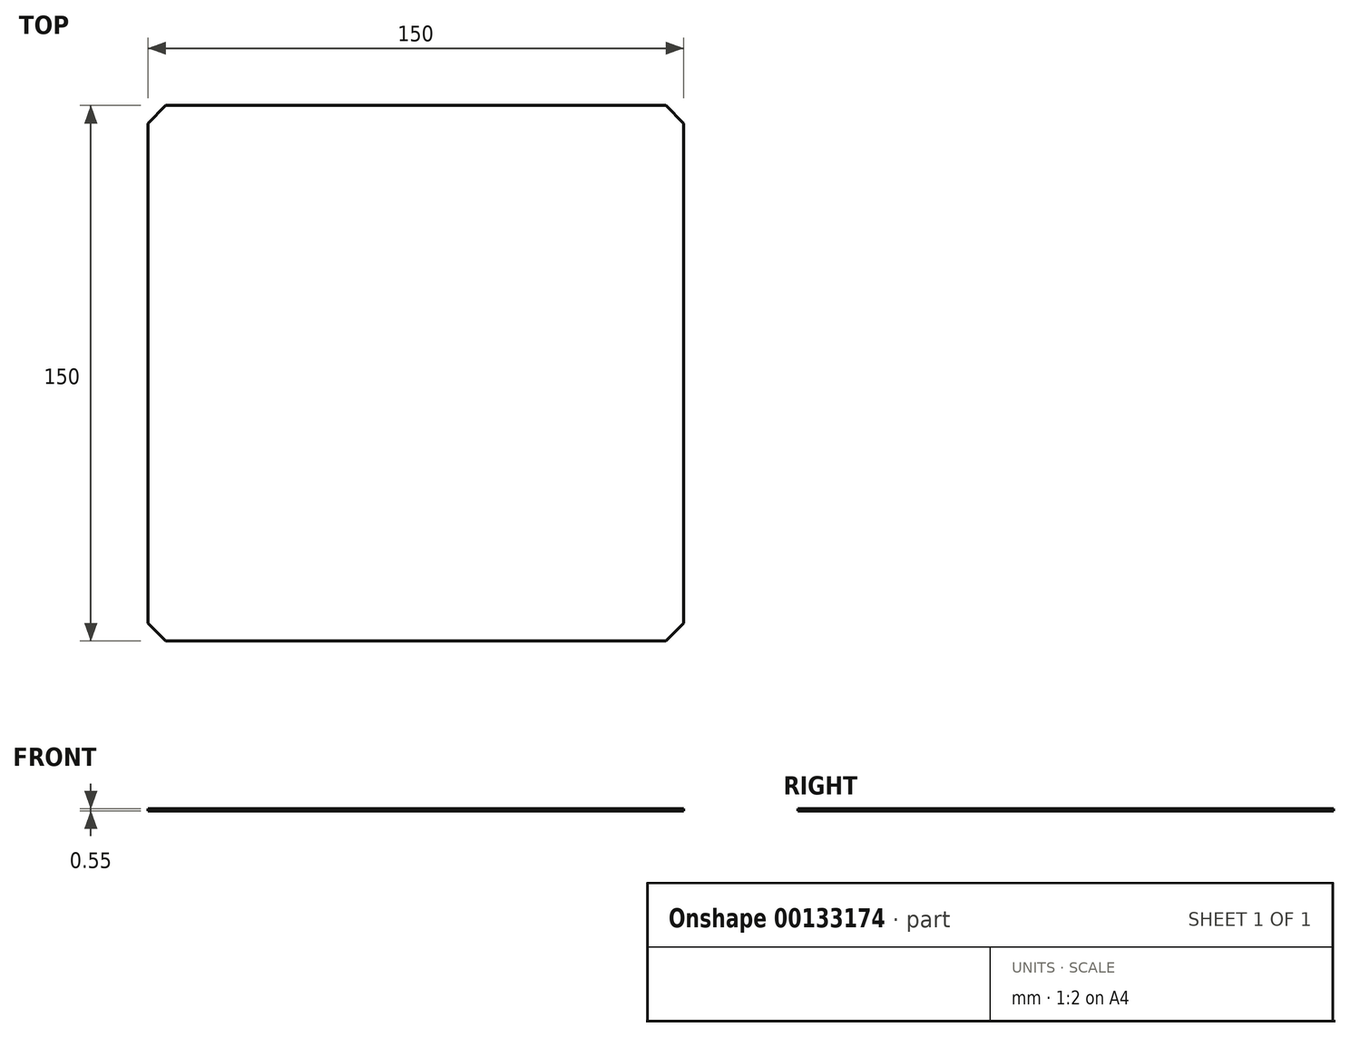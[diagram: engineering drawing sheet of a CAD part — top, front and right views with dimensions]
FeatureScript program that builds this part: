
annotation { "Feature Type Name" : "Feature", "Feature Type Description" : "" }
export const myFeature = defineFeature(function(context is Context, id is Id, definition is map)
    precondition{}
    {
        {
            var Q0;
            Q0=qCreatedBy(makeId("Top.planeOp"),FACE);
            var sketch = newSketch(context, id + "F0", { "sketchPlane" : qUnion([Q0])});
            skLineSegment(sketch, "E0.bottom", {"start": v(-75, 75) * mm, "end": v(75, 75) * mm});
            skLineSegment(sketch, "E0.top", {"start": v(-75, -75) * mm, "end": v(75, -75) * mm});
            skLineSegment(sketch, "E0.left", {"start": v(-75, 75) * mm, "end": v(-75, -75) * mm});
            skLineSegment(sketch, "E0.right", {"start": v(75, 75) * mm, "end": v(75, -75) * mm});
            skPoint(sketch, "E0.middle", {"position": v(0, 0) * mm});
            skSolve(sketch);
        }
        {
            var Q0;
            Q0 = qSketchRegion(id + "F0", true);
            extrude(context, id + "F1", {"entities" : qUnion([Q0]), "depth" : .55 * mm});
        }
        {
            var Q0;
            Q0=makeQuery(id+"F1.opExtrude","SWEPT_EDGE",EDGE,{"disambiguationData":[OSD([sQuery(id+"F0.wireOp",EDGE,"E0.top"),sQuery(id+"F0.wireOp",EDGE,"E0.left")])]});
            var Q1;
            Q1=makeQuery(id+"F1.opExtrude","SWEPT_EDGE",EDGE,{"disambiguationData":[OSD([sQuery(id+"F0.wireOp",EDGE,"E0.bottom"),sQuery(id+"F0.wireOp",EDGE,"E0.left")])]});
            var Q2;
            Q2=makeQuery(id+"F1.opExtrude","SWEPT_EDGE",EDGE,{"disambiguationData":[OSD([sQuery(id+"F0.wireOp",EDGE,"E0.bottom"),sQuery(id+"F0.wireOp",EDGE,"E0.right")])]});
            var Q3;
            Q3=makeQuery(id+"F1.opExtrude","SWEPT_EDGE",EDGE,{"disambiguationData":[OSD([sQuery(id+"F0.wireOp",EDGE,"E0.top"),sQuery(id+"F0.wireOp",EDGE,"E0.right")])]});
            chamfer(context, id + "F2", {"entities" : qUnion([Q0, Q1, Q2, Q3]), "width" : 5 * mm, "tangentPropagation" : true});
        }
    });
